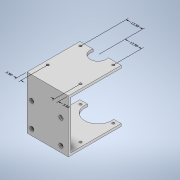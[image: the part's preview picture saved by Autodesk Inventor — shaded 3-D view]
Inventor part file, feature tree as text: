
AUTODESK INVENTOR PART (.ipt)
format: ipt  version: 2022 (Build 260153000, 153)  size: 174,080 bytes
history: native  units: mm
features: sketch x6, other x5, extrude x4, hole x2
ambient origin geometry x8: Origin, YZ Plane, XZ Plane, XY Plane, X Axis, Y Axis, Z Axis, Center Point
bodies: Body1 (feature_tree)
feature tree (17):
  other  "ソリッド1"
  extrude  "押し出し1"  Depth=43.5mm
  extrude  "押し出し2"  Depth=34.0mm
  extrude  "押し出し3"  Depth=43.5mm TaperAngle=0.0deg
  extrude  "押し出し4"  Depth=2.0mm
  hole  "穴1"  [1 undecoded]
  hole  "穴2"  [1 undecoded]
  sketch  "スケッチ1"
  sketch  "スケッチ2"
  sketch  "スケッチ3"
  sketch  "スケッチ4"
  sketch  "スケッチ5"
  sketch  "スケッチ6"
  other  "長さ寸法 1"
  other  "長さ寸法 2"
  other  "長さ寸法 3"
  other  "長さ寸法 4"
note: 2 required parameter values undecoded (feature->parameter linkage not recoverable at this tier; creation-order binding heuristic only, values carry confidence <= 0.55)
